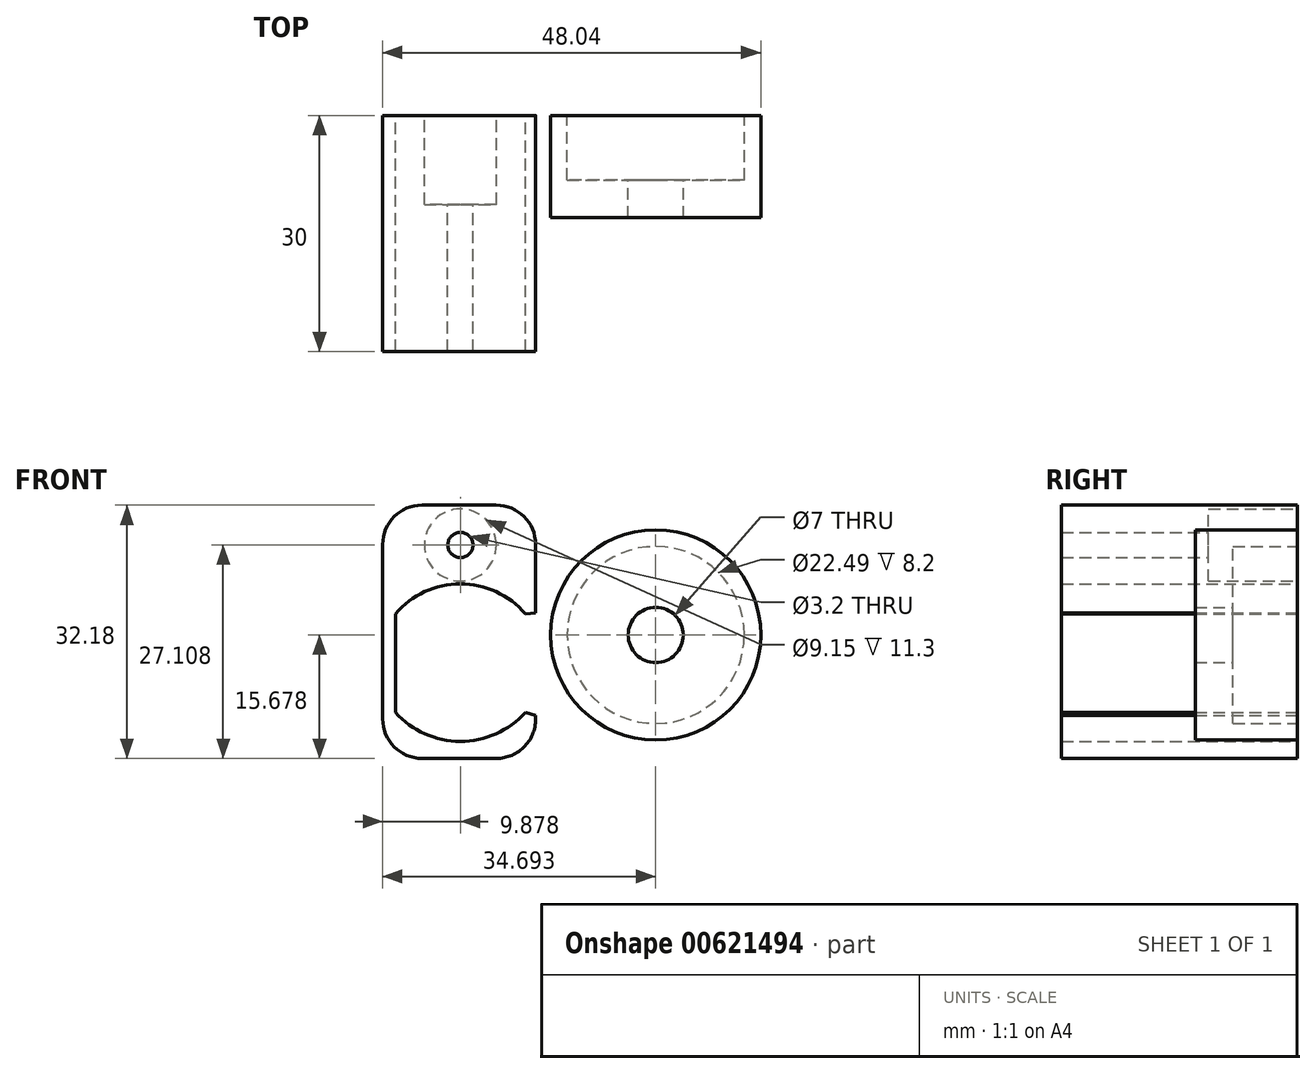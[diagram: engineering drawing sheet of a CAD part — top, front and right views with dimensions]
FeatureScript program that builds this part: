
annotation { "Feature Type Name" : "Feature", "Feature Type Description" : "" }
export const myFeature = defineFeature(function(context is Context, id is Id, definition is map)
    precondition{}
    {
        {
            var Q0;
            Q0=qCreatedBy(makeId("Front.planeOp"),FACE);
            var sketch = newSketch(context, id + "F0", { "sketchPlane" : qUnion([Q0])});
            skPoint(sketch, "E0.middle", {"position": v(-5.05, 1.08) * mm});
            skLineSegment(sketch, "E1.trimOffspring", {"start": v(-13.3, -5.19) * mm, "end": v(-13.3, 7.34) * mm});
            skLineSegment(sketch, "E2.bottom", {"start": v(-9.93, 21.15) * mm, "end": v(-0.5, 21.15) * mm});
            skLineSegment(sketch, "E2.top", {"start": v(-9.93, -11.03) * mm, "end": v(-0.48, -11.03) * mm});
            skLineSegment(sketch, "E2.left", {"start": v(-14.93, 16.15) * mm, "end": v(-14.93, -6.03) * mm});
            skLineSegment(sketch, "E3", {"start": v(4.5, 16.15) * mm, "end": v(4.5, 7.44) * mm});
            skLineSegment(sketch, "E4", {"start": v(4.5, 7.44) * mm, "end": v(3.2, 7.34) * mm});
            skLineSegment(sketch, "E5", {"start": v(4.5, -5.54) * mm, "end": v(4.5, -5.77) * mm});
            skCircle(sketch, "E6", {"center": v(-5.05, 16.08) * mm, "radius": 1.6 * mm});
            skPoint(sketch, "E7.visualSharp", {"position": v(-14.93, 21.15) * mm});
            skArc(sketch, "E7.filletArc", {"start": v(-9.93, 21.15) * mm, "mid": v(-13.46, 19.69) * mm, "end": v(-14.93, 16.15) * mm});
            skPoint(sketch, "E8.visualSharp", {"position": v(4.5, 21.15) * mm});
            skArc(sketch, "E8.filletArc", {"start": v(4.5, 16.15) * mm, "mid": v(3.03, 19.69) * mm, "end": v(-0.5, 21.15) * mm});
            skPoint(sketch, "E9.visualSharp", {"position": v(-14.93, -11.03) * mm});
            skArc(sketch, "E9.filletArc", {"start": v(-14.93, -6.03) * mm, "mid": v(-13.46, -9.57) * mm, "end": v(-9.93, -11.03) * mm});
            skPoint(sketch, "E10.visualSharp", {"position": v(4.79, -11.03) * mm});
            skArc(sketch, "E10.filletArc", {"start": v(-0.48, -11.03) * mm, "mid": v(3.14, -9.47) * mm, "end": v(4.5, -5.77) * mm});
            skCircle(sketch, "E11", {"center": v(-5.05, 16.08) * mm, "radius": 4.58 * mm});
            skLineSegment(sketch, "E12", {"start": v(4.5, -5.54) * mm, "end": v(3.2, -5.19) * mm});
            skArc(sketch, "E13", {"start": v(3.2, 7.34) * mm, "mid": v(-5.05, 11.14) * mm, "end": v(-13.3, 7.34) * mm});
            skArc(sketch, "E14", {"start": v(-13.3, -5.19) * mm, "mid": v(-5.05, -8.87) * mm, "end": v(3.2, -5.19) * mm});
            skSolve(sketch);
        }
        {
            var Q0;
            Q0=makeQuery(id+"F0.imprint","IMPRINT",FACE,{"disambiguationData":[TD([[makeQuery(id+"F0.imprint","IMPRINT",EDGE,{"derivedFrom":sQuery(id+"F0.wireOp",EDGE,"19c14067-8f59-4f57-81ee-abd91a3b8462")}),-1.0]])]});
            var Q1;
            Q1=makeQuery(id+"F0.imprint","IMPRINT",FACE,{"disambiguationData":[TD([[makeQuery(id+"F0.imprint","IMPRINT",EDGE,{"derivedFrom":sQuery(id+"F0.wireOp",EDGE,"E6")}),-1.0]])]});
            var Q2;
            Q2=makeQuery(id+"F0.imprint","IMPRINT",FACE,{"disambiguationData":[TD([[makeQuery(id+"F0.imprint","IMPRINT",EDGE,{"derivedFrom":sQuery(id+"F0.wireOp",EDGE,"E1.trimOffspring")}),1.0]])]});
            extrude(context, id + "F1", {"entities" : qUnion([Q0, Q1, Q2]), "depth" : 30 * mm, "offsetDistance" : 25 * mm});
        }
        {
            var Q0;
            Q0=qCreatedBy(makeId("Front.planeOp"),FACE);
            var sketch = newSketch(context, id + "F2", { "sketchPlane" : qUnion([Q0])});
            skCircle(sketch, "E15", {"center": v(19.76, 4.65) * mm, "radius": 13.35 * mm});
            skCircle(sketch, "E16", {"center": v(19.76, 4.65) * mm, "radius": 3.5 * mm});
            skCircle(sketch, "E17", {"center": v(19.76, 4.65) * mm, "radius": 11.25 * mm});
            skSolve(sketch);
        }
        {
            var Q0;
            Q0=makeQuery(id+"F2.imprint","IMPRINT",FACE,{"disambiguationData":[TD([[makeQuery(id+"F2.imprint","IMPRINT",EDGE,{"derivedFrom":sQuery(id+"F2.wireOp",EDGE,"E15")}),1.0]])]});
            var Q1;
            Q1=makeQuery(id+"F2.imprint","IMPRINT",FACE,{"disambiguationData":[TD([[makeQuery(id+"F2.imprint","IMPRINT",EDGE,{"derivedFrom":sQuery(id+"F2.wireOp",EDGE,"E16")}),-1.0]])]});
            extrude(context, id + "F3", {"entities" : qUnion([Q0, Q1]), "depth" : 13 * mm, "offsetDistance" : 25 * mm});
        }
        {
            var Q0;
            Q0=makeQuery(id+"F2.imprint","IMPRINT",FACE,{"disambiguationData":[TD([[makeQuery(id+"F2.imprint","IMPRINT",EDGE,{"derivedFrom":sQuery(id+"F2.wireOp",EDGE,"E16")}),-1.0]])]});
            extrude(context, id + "F4", {"entities" : qUnion([Q0]), "operationType" : NewBodyOperationType.REMOVE, "depth" : 8.2 * mm, "offsetDistance" : 25 * mm});
        }
        {
            var Q0;
            Q0=makeQuery(id+"F0.imprint","IMPRINT",FACE,{"disambiguationData":[TD([[makeQuery(id+"F0.imprint","IMPRINT",EDGE,{"derivedFrom":sQuery(id+"F0.wireOp",EDGE,"E6")}),-1.0]])]});
            extrude(context, id + "F5", {"entities" : qUnion([Q0]), "operationType" : NewBodyOperationType.REMOVE, "depth" : 11.3 * mm, "offsetDistance" : 25 * mm});
        }
    });
